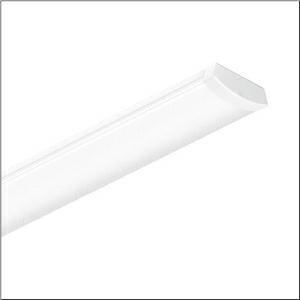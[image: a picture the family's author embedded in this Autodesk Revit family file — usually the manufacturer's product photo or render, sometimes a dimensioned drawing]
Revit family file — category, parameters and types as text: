
# Revit family: siluette_r__21_51ln12mnm70a_66ce
name_source: partatom
category: Lighting Fixtures
units: mm (PartAtom-declared; Revit-internal decimal feet)

## family parameters
Cut with Voids When Loaded = No
Host = Face
Light Source = No
Part Type = Normal
Room Calculation Point = No
Round Connector Dimension = Use Diameter
Shared = No

## types (1)
- --- (1 x LED, 4320 lm, 28.8 W, 5000K)
    Apparent Load = 29 VA
    CIE Flux Codes = 43 73 92 94 100
    Color Rendering = 80
    Color Temperature = 5000K
    Default Elevation = 1800 mm
    Description = Siluette® 21, office luminaire, primary optical cover: enclosure, of PC, frosted, light emission: direct distribution, primary light characteristic: symmetric, installation type: suspended mounting, surface-mounted, LED, rated luminous flux: 7.150lm, luminous efficacy: 147lm/W, light colour: 830/840/850, colour temperature: 3000/4000/5000K, control gear: ON/OFF Multilumen, with terminal, 3-pole, mains connection: 220..240V, AC, 50/60Hz, rated input power: 49W, housing, of sheet steel, white, length: 1.500mm, width: 152mm, height: 53mm, end cap, of PMMA, white, protection rating (complete): IP44, insulation class (complete): insulation class I (protective earthing), certification: CE, UKCA, protection symbol: D, impact resistance: IK04, permissible operating ambient temperature: -20..+40°C, contact your sales advisor before using the luminaires in applications with unclear chemical exposure, large temperature fluctuations or condensation-forming humidity, corresponds to IFS (International Featured Standards) requirements for safety and quality in the food industry, packaging unit: 1 piece
    Height = 52 mm  [stored 0.170604 ft]
    Lamp = 1 x LED
    Lamp Light Flux = 4320 lm
    Lamp Power = 28.8 W
    Lamp count = 1
    Length = 1485 mm
    Luminous efficacy = 150 lm/W
    Manufacturer = Siteco
    ModVariant = No
    Model = 51LN12MNM70A
    Mounting Place = Ceiling
    Mounting Type = Pendant
    Number of Poles = 1
    OnlyDefault = Yes
    Power Factor = 1
    Product Name = Siluette® 21
    Product group = office luminaire | ceiling pendant
    ProductGroupID = 903
    Protection Class = Protection class I
    Protection Degree = IP 44
    RLX_Detail_Level = 1
    RLX_Emergency_Light_Flux = 0 lm
    RLX_Emergency_Type = 0
    RLX_Emergency_Type_DB = No
    RlxData = <blob elided: 19213 chars, md5=40d5eae5>
    Socket = socket
    Standby Power = 0 W
    System Light Flux = 4320 lm
    System Power = 29 W
    Type Comments = individual setting: colour temperature 5000K, luminous flux: 61 % | (OFF | OFF | ON) | 200 mA
    Type Image = l_1296910.jpg
    URL = http://relux.com
    VarID = @adj_079503
    Voltage = 0 V
    Weight = 0.00 kg
    Width = 152 mm

note: [stored X ft] marks values corroborated as IEEE doubles in the binary element streams (Revit-internal decimal feet)

## geometry (parser evidence)
native form markers: Blend x4, Sweep x14
no freeform markers — native parametric forms only
